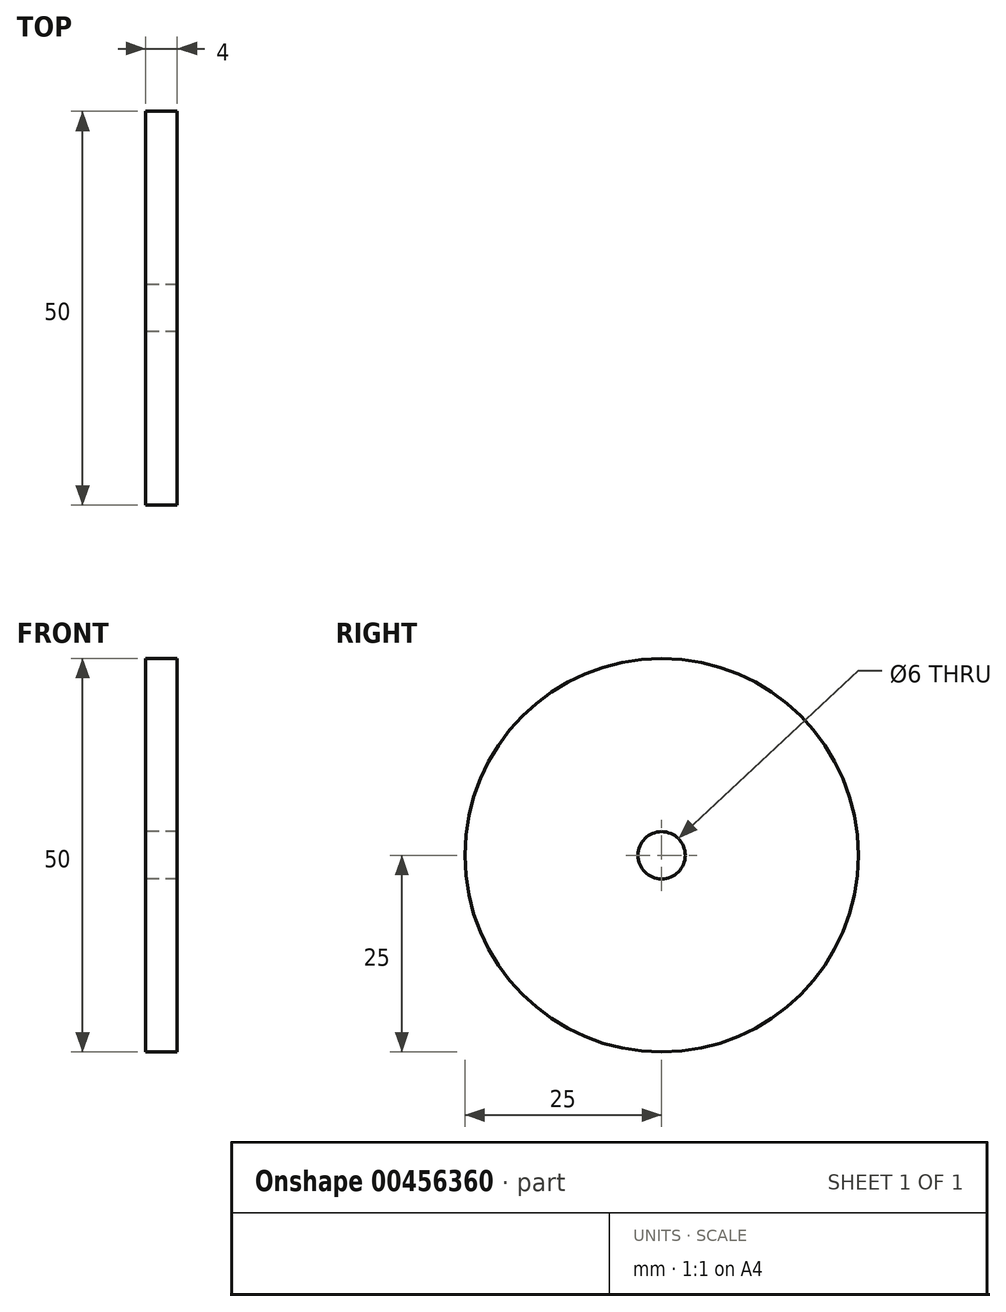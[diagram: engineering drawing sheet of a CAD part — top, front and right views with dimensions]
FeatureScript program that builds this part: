
annotation { "Feature Type Name" : "Feature", "Feature Type Description" : "" }
export const myFeature = defineFeature(function(context is Context, id is Id, definition is map)
    precondition{}
    {
        {
            var Q0;
            Q0=qCreatedBy(makeId("Right.planeOp"),FACE);
            var sketch = newSketch(context, id + "F0", { "sketchPlane" : qUnion([Q0])});
            skCircle(sketch, "E0", {"center": v(0, 0) * mm, "radius": 25 * mm});
            skCircle(sketch, "E1", {"center": v(0, 0) * mm, "radius": 3 * mm});
            skSolve(sketch);
        }
        {
            var Q0;
            Q0=makeQuery(id+"F0.imprint","IMPRINT",FACE,{"disambiguationData":[TD([[makeQuery(id+"F0.imprint","IMPRINT",EDGE,{"derivedFrom":sQuery(id+"F0.wireOp",EDGE,"E0")}),1.0]])]});
            extrude(context, id + "F1", {"entities" : qUnion([Q0]), "depth" : 2 * mm, "hasSecondDirection" : true, "secondDirectionOppositeDirection" : true, "secondDirectionDepth" : 2 * mm});
        }
    });
